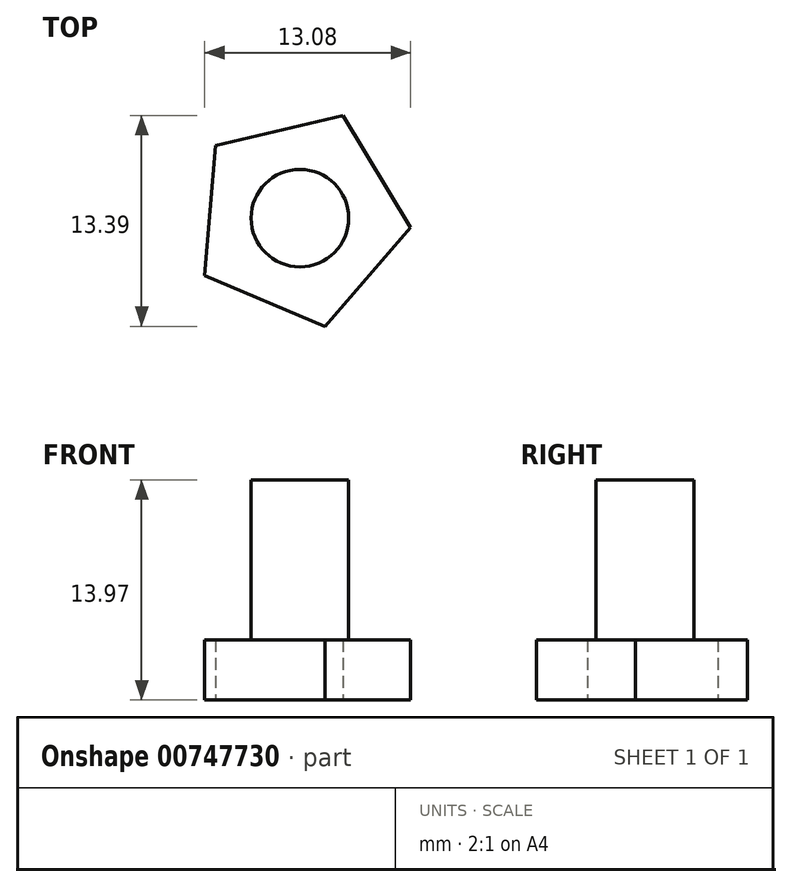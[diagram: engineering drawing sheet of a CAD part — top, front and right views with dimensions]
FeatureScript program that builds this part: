
annotation { "Feature Type Name" : "Feature", "Feature Type Description" : "" }
export const myFeature = defineFeature(function(context is Context, id is Id, definition is map)
    precondition{}
    {
        {
            var Q0;
            Q0=qCreatedBy(makeId("Top.planeOp"),FACE);
            var sketch = newSketch(context, id + "F0", { "sketchPlane" : qUnion([Q0])});
            skCircle(sketch, "E0", {"center": v(0, 0) * mm, "radius": 3.1 * mm});
            skCircle(sketch, "E1.cCircle", {"center": v(0, 0) * mm, "radius": 5.72 * mm, "construction": true});
            skLineSegment(sketch, "E1.0", {"start": v(2.74, 6.51) * mm, "end": v(7.04, -0.6) * mm});
            skLineSegment(sketch, "E1.1", {"start": v(7.04, -0.6) * mm, "end": v(1.6, -6.88) * mm});
            skLineSegment(sketch, "E1.2", {"start": v(1.6, -6.88) * mm, "end": v(-6.04, -3.66) * mm});
            skLineSegment(sketch, "E1.3", {"start": v(-6.04, -3.66) * mm, "end": v(-5.34, 4.62) * mm});
            skLineSegment(sketch, "E1.4", {"start": v(-5.34, 4.62) * mm, "end": v(2.74, 6.51) * mm});
            skPoint(sketch, "E1.0.midPoint", {"position": v(4.9, 2.96) * mm});
            skSolve(sketch);
        }
        {
            var Q0;
            Q0=makeQuery(id+"F0.imprint","IMPRINT",FACE,{"disambiguationData":[TD([[makeQuery(id+"F0.imprint","IMPRINT",EDGE,{"derivedFrom":sQuery(id+"F0.wireOp",EDGE,"E0")}),1.0]])]});
            extrude(context, id + "F1", {"entities" : qUnion([Q0]), "depth" : 13.97 * mm, "offsetDistance" : 25.4 * mm});
        }
        {
            var Q0;
            Q0=makeQuery(id+"F0.imprint","IMPRINT",FACE,{"disambiguationData":[TD([[makeQuery(id+"F0.imprint","IMPRINT",EDGE,{"derivedFrom":sQuery(id+"F0.wireOp",EDGE,"E0")}),-1.0]])]});
            extrude(context, id + "F2", {"entities" : qUnion([Q0]), "operationType" : NewBodyOperationType.ADD, "depth" : 3.8 * mm, "offsetDistance" : 25.4 * mm});
        }
    });
